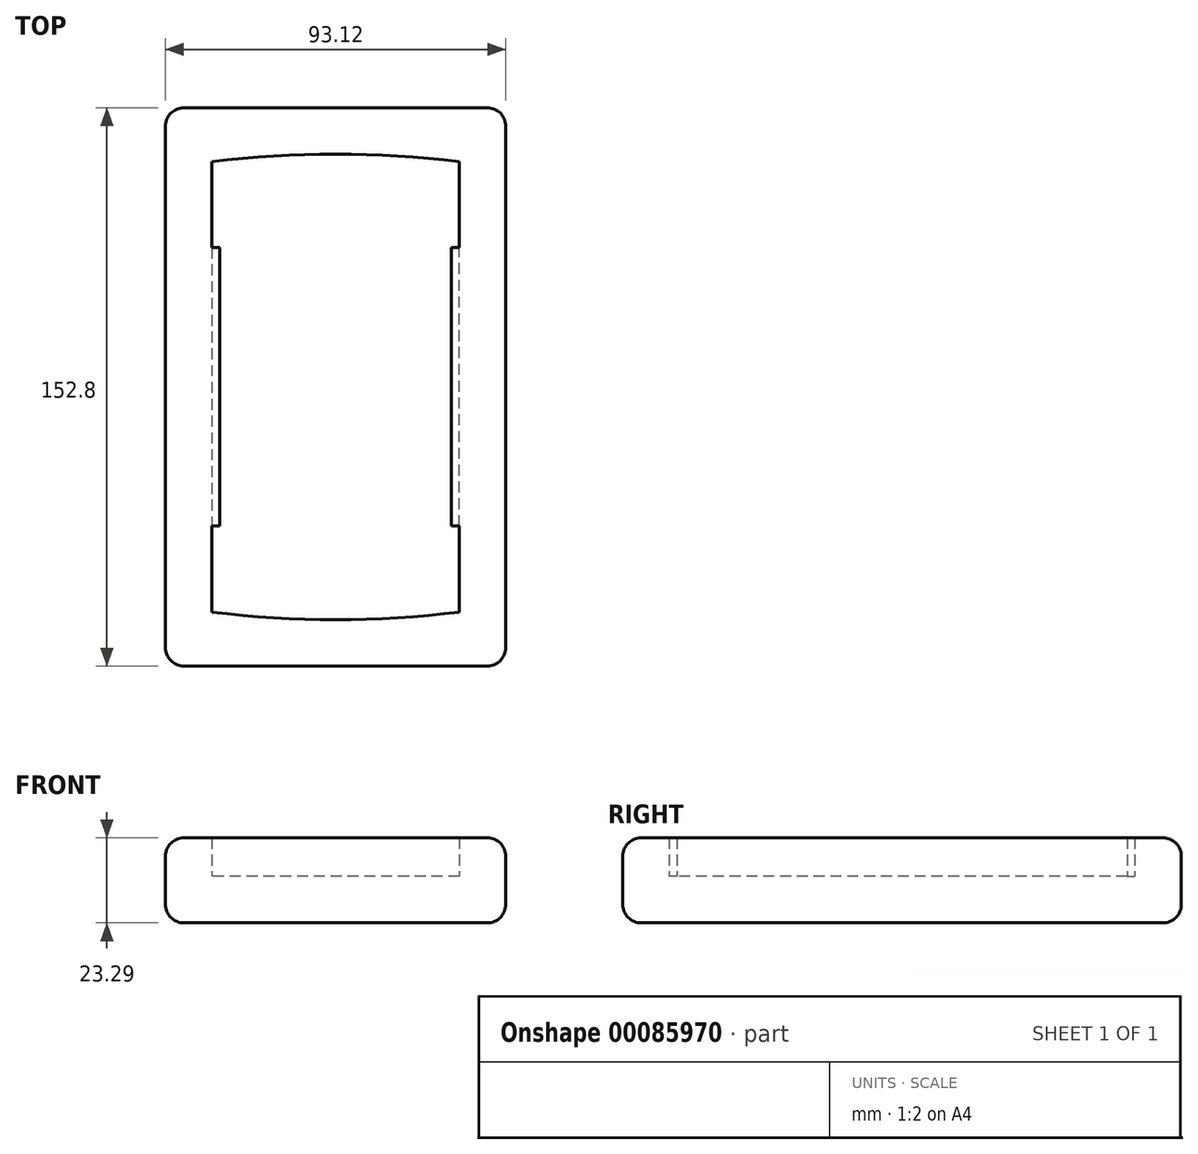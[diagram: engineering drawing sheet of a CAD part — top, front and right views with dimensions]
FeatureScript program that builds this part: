
annotation { "Feature Type Name" : "Feature", "Feature Type Description" : "" }
export const myFeature = defineFeature(function(context is Context, id is Id, definition is map)
    precondition{}
    {
        {
            var Q0;
            Q0=qCreatedBy(makeId("Top.planeOp"),FACE);
            var sketch = newSketch(context, id + "F0", { "sketchPlane" : qUnion([Q0])});
            skLineSegment(sketch, "E0.left", {"start": v(33.86, 61.62) * mm, "end": v(33.86, -61.62) * mm});
            skLineSegment(sketch, "E0.right", {"start": v(-33.86, 61.62) * mm, "end": v(-33.86, -61.62) * mm});
            skPoint(sketch, "E0.middle", {"position": v(0, 0) * mm});
            skLineSegment(sketch, "E1.bottom", {"start": v(0, 63.7) * mm, "end": v(0, 63.7) * mm});
            skLineSegment(sketch, "E1.top", {"start": v(0, -63.7) * mm, "end": v(0, -63.7) * mm});
            skArc(sketch, "E2", {"start": v(33.86, 61.62) * mm, "mid": v(0, 63.7) * mm, "end": v(-33.86, 61.62) * mm});
            skArc(sketch, "E3", {"start": v(-33.86, -61.62) * mm, "mid": v(0, -63.7) * mm, "end": v(33.86, -61.62) * mm});
            skLineSegment(sketch, "E4.bottom", {"start": v(46.56, 76.4) * mm, "end": v(-46.56, 76.4) * mm});
            skLineSegment(sketch, "E4.top", {"start": v(46.56, -76.4) * mm, "end": v(-46.56, -76.4) * mm});
            skLineSegment(sketch, "E4.left", {"start": v(46.56, 76.4) * mm, "end": v(46.56, -76.4) * mm});
            skLineSegment(sketch, "E4.right", {"start": v(-46.56, 76.4) * mm, "end": v(-46.56, -76.4) * mm});
            skSolve(sketch);
        }
        {
            var Q0;
            Q0=makeQuery(id+"F0.imprint","IMPRINT",FACE,{"disambiguationData":[TD([[makeQuery(id+"F0.imprint","IMPRINT",EDGE,{"derivedFrom":sQuery(id+"F0.wireOp",EDGE,"E0.left")}),-1.0]])]});
            extrude(context, id + "F1", {"entities" : qUnion([Q0]), "depth" : 12.7 * mm});
        }
        {
            var Q0;
            Q0=makeQuery(id+"F0.imprint","IMPRINT",FACE,{"disambiguationData":[TD([[makeQuery(id+"F0.imprint","IMPRINT",EDGE,{"derivedFrom":sQuery(id+"F0.wireOp",EDGE,"E0.left")}),1.0]])]});
            extrude(context, id + "F2", {"entities" : qUnion([Q0]), "operationType" : NewBodyOperationType.ADD, "depth" : 23.3 * mm});
        }
        {
            var Q0;
            Q0=makeQuery(id+"F2.opExtrude","SWEPT_FACE",FACE,{"disambiguationData":[OSD([sQuery(id+"F0.wireOp",EDGE,"E4.bottom")])]});
            var Q1;
            Q1=makeQuery(id+"F2.opExtrude","SWEPT_FACE",FACE,{"disambiguationData":[OSD([sQuery(id+"F0.wireOp",EDGE,"E4.left")])]});
            var Q2;
            Q2=makeQuery(id+"F2.opExtrude","SWEPT_FACE",FACE,{"disambiguationData":[OSD([sQuery(id+"F0.wireOp",EDGE,"E4.right")])]});
            var Q3;
            {var subQ0=sQuery(id+"F0.wireOp",EDGE,"E3");var subQ1=sQuery(id+"F0.wireOp",EDGE,"E2");var subQ2=sQuery(id+"F0.wireOp",EDGE,"E0.right");var subQ3=sQuery(id+"F0.wireOp",EDGE,"E0.left");Q3=makeQuery(id+"F2.boolean.opBoolean","MERGE",FACE,{"derivedFrom":[makeQuery(id+"F1.opExtrude","CAP_FACE",FACE,{"disambiguationData":[OSD([subQ3,subQ2,subQ1,subQ0])],"isStart":true}),makeQuery(id+"F2.opExtrude","CAP_FACE",FACE,{"disambiguationData":[OSD([subQ3,subQ2,subQ1,subQ0,sQuery(id+"F0.wireOp",EDGE,"E4.bottom"),sQuery(id+"F0.wireOp",EDGE,"E4.top"),sQuery(id+"F0.wireOp",EDGE,"E4.left"),sQuery(id+"F0.wireOp",EDGE,"E4.right")])],"isStart":true})]});}
            var Q4;
            Q4=makeQuery(id+"F2.opExtrude","SWEPT_FACE",FACE,{"disambiguationData":[OSD([sQuery(id+"F0.wireOp",EDGE,"E4.top")])]});
            fillet(context, id + "F3", {"entities" : qUnion([Q0, Q1, Q2, Q3, Q4]), "radius" : 5.08 * mm, "tangentPropagation" : true, "allowEdgeOverflow" : false});
        }
        {
            var Q0;
            Q0=makeQuery(id+"F2.opExtrude","SWEPT_FACE",FACE,{"disambiguationData":[OSD([sQuery(id+"F0.wireOp",EDGE,"E0.right")])]});
            var sketch = newSketch(context, id + "F4", { "sketchPlane" : qUnion([Q0])});
            skLineSegment(sketch, "E5.bottom", {"start": v(38.13, 23.3) * mm, "end": v(-38.07, 23.3) * mm});
            skLineSegment(sketch, "E5.top", {"start": v(38.13, 23.24) * mm, "end": v(-38.07, 23.24) * mm});
            skLineSegment(sketch, "E5.left", {"start": v(38.13, 23.3) * mm, "end": v(38.13, 23.24) * mm});
            skLineSegment(sketch, "E5.right", {"start": v(-38.07, 23.3) * mm, "end": v(-38.07, 23.24) * mm});
            skPoint(sketch, "E5.middle", {"position": v(0.03, 23.27) * mm});
            skSolve(sketch);
        }
        {
            var Q0;
            Q0 = qSketchRegion(id + "F4", true);
            extrude(context, id + "F5", {"entities" : qUnion([Q0]), "operationType" : NewBodyOperationType.ADD, "depth" : 2.16 * mm});
        }
        {
            var Q0;
            Q0=makeQuery(id+"F2.opExtrude","SWEPT_FACE",FACE,{"disambiguationData":[OSD([sQuery(id+"F0.wireOp",EDGE,"E0.left")])]});
            var sketch = newSketch(context, id + "F6", { "sketchPlane" : qUnion([Q0])});
            skLineSegment(sketch, "E6.bottom", {"start": v(38.1, 23.3) * mm, "end": v(-38.1, 23.3) * mm});
            skLineSegment(sketch, "E6.top", {"start": v(38.1, 23.24) * mm, "end": v(-38.1, 23.24) * mm});
            skLineSegment(sketch, "E6.left", {"start": v(38.1, 23.3) * mm, "end": v(38.1, 23.24) * mm});
            skLineSegment(sketch, "E6.right", {"start": v(-38.1, 23.3) * mm, "end": v(-38.1, 23.24) * mm});
            skPoint(sketch, "E6.middle", {"position": v(0, 23.27) * mm});
            skSolve(sketch);
        }
        {
            var Q0;
            Q0 = qSketchRegion(id + "F6", true);
            extrude(context, id + "F7", {"entities" : qUnion([Q0]), "operationType" : NewBodyOperationType.ADD, "depth" : 2.16 * mm});
        }
    });
